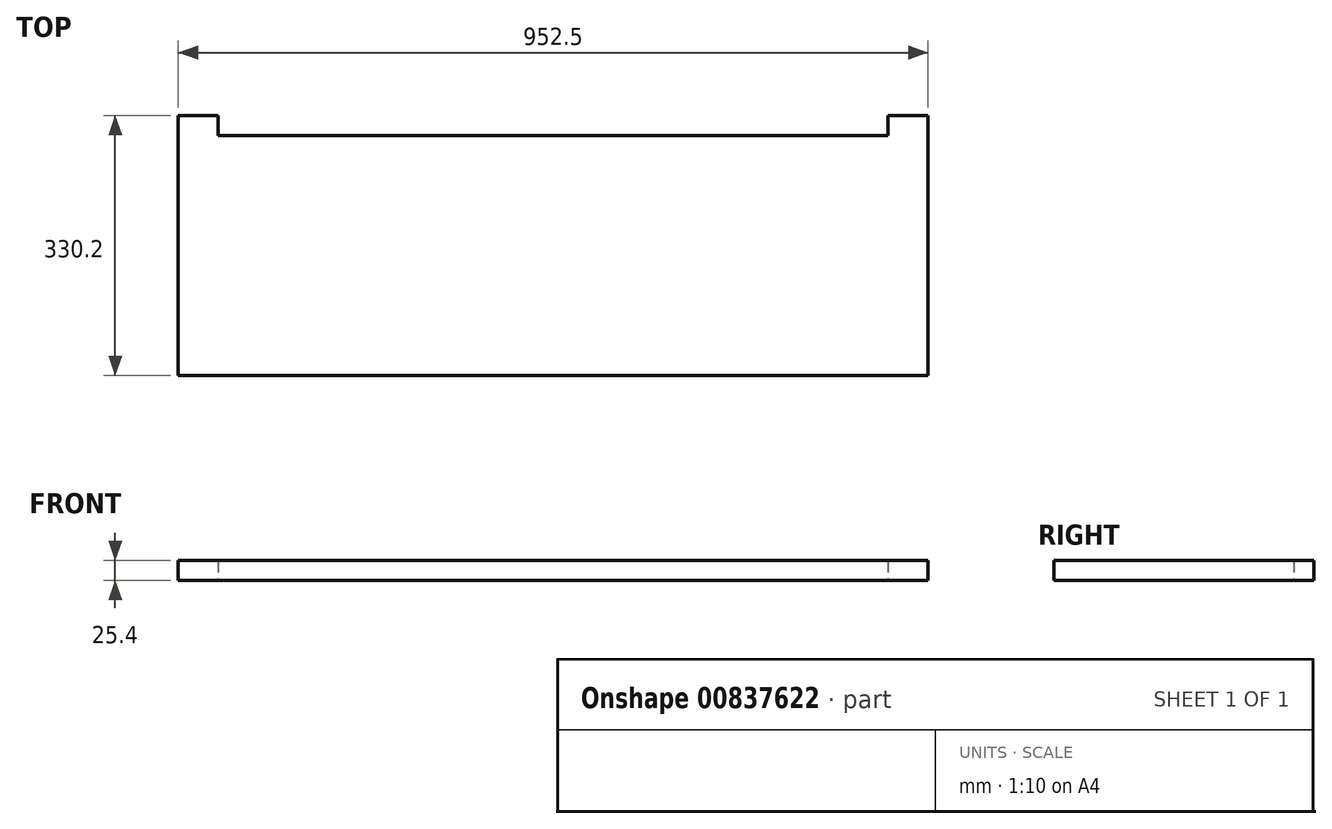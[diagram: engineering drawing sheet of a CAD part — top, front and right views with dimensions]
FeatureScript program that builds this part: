
annotation { "Feature Type Name" : "Feature", "Feature Type Description" : "" }
export const myFeature = defineFeature(function(context is Context, id is Id, definition is map)
    precondition{}
    {
        {
            var Q0;
            Q0=qCreatedBy(makeId("Top.planeOp"),FACE);
            var sketch = newSketch(context, id + "F0", { "sketchPlane" : qUnion([Q0])});
            skLineSegment(sketch, "E0.bottom", {"start": v(476.25, -165.1) * mm, "end": v(-476.25, -165.1) * mm});
            skLineSegment(sketch, "E0.top", {"start": v(476.25, 165.1) * mm, "end": v(425.45, 165.1) * mm});
            skLineSegment(sketch, "E0.left", {"start": v(476.25, -165.1) * mm, "end": v(476.25, 165.1) * mm});
            skLineSegment(sketch, "E0.right", {"start": v(-476.25, -165.1) * mm, "end": v(-476.25, 165.1) * mm});
            skPoint(sketch, "E0.middle", {"position": v(0, 0) * mm});
            skLineSegment(sketch, "E1.top", {"start": v(-425.45, 139.7) * mm, "end": v(425.45, 139.7) * mm});
            skLineSegment(sketch, "E1.left", {"start": v(-425.45, 165.1) * mm, "end": v(-425.45, 139.7) * mm});
            skLineSegment(sketch, "E1.right", {"start": v(425.45, 165.1) * mm, "end": v(425.45, 139.7) * mm});
            skLineSegment(sketch, "E2.trimOffspring", {"start": v(-425.45, 165.1) * mm, "end": v(-476.25, 165.1) * mm});
            skSolve(sketch);
        }
        {
            var Q0;
            Q0 = qSketchRegion(id + "F0", true);
            extrude(context, id + "F1", {"entities" : qUnion([Q0]), "depth" : 25.4 * mm, "offsetDistance" : 25.4 * mm});
        }
    });
